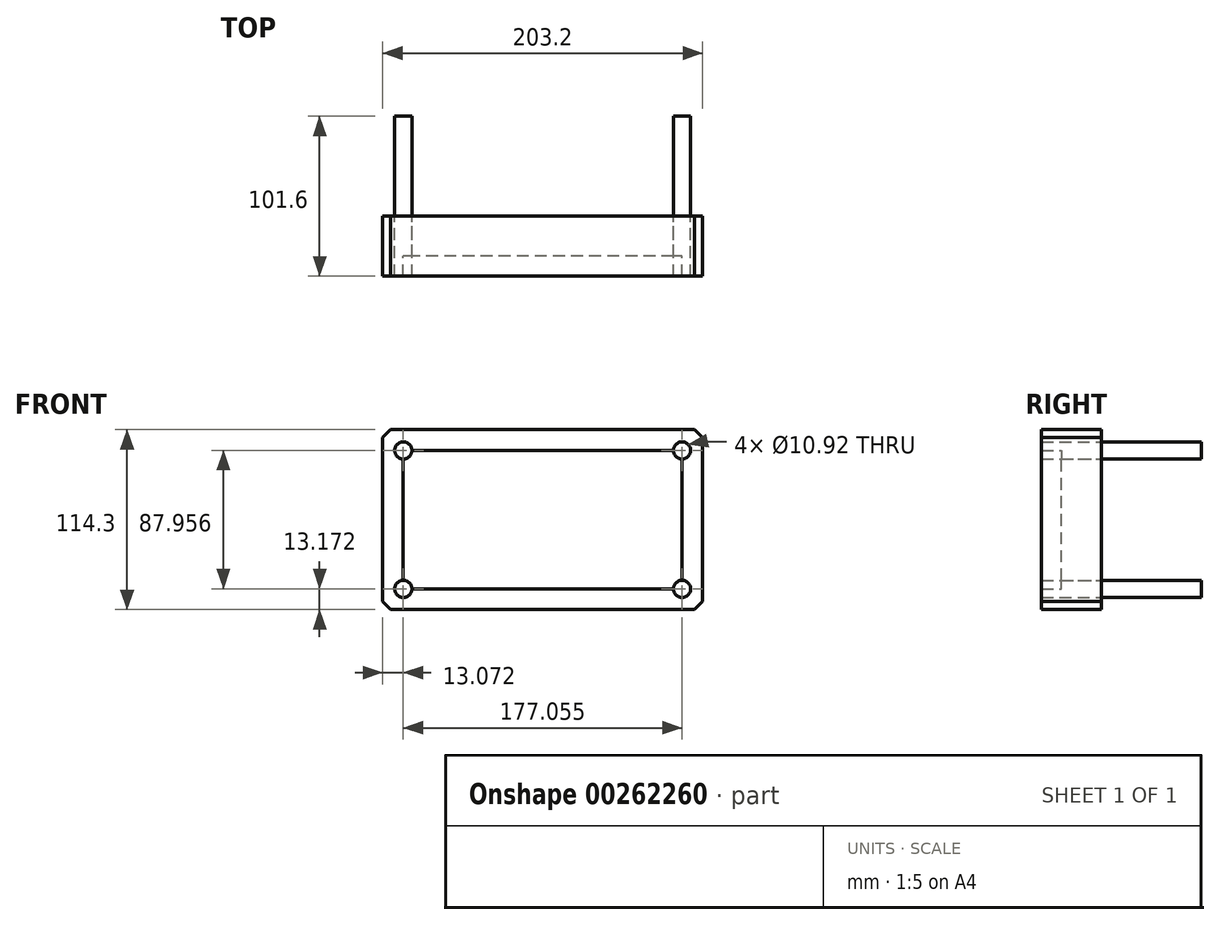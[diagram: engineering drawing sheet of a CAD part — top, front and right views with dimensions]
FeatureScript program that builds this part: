
annotation { "Feature Type Name" : "Feature", "Feature Type Description" : "" }
export const myFeature = defineFeature(function(context is Context, id is Id, definition is map)
    precondition{}
    {
        {
            var Q0;
            Q0=qCreatedBy(makeId("Front.planeOp"),FACE);
            var sketch = newSketch(context, id + "F0", { "sketchPlane" : qUnion([Q0])});
            skLineSegment(sketch, "E0.bottom", {"start": v(101.6, 57.15) * mm, "end": v(-101.6, 57.15) * mm});
            skLineSegment(sketch, "E0.top", {"start": v(101.6, -57.15) * mm, "end": v(-101.6, -57.15) * mm});
            skLineSegment(sketch, "E0.left", {"start": v(101.6, 57.15) * mm, "end": v(101.6, -57.15) * mm});
            skLineSegment(sketch, "E0.right", {"start": v(-101.6, 57.15) * mm, "end": v(-101.6, -57.15) * mm});
            skPoint(sketch, "E0.middle", {"position": v(0, 0) * mm});
            skLineSegment(sketch, "E1.bottom", {"start": v(88.53, -43.98) * mm, "end": v(-88.53, -43.98) * mm});
            skLineSegment(sketch, "E1.top", {"start": v(88.53, 43.98) * mm, "end": v(-88.53, 43.98) * mm});
            skLineSegment(sketch, "E1.left", {"start": v(88.53, -43.98) * mm, "end": v(88.53, 43.98) * mm});
            skLineSegment(sketch, "E1.right", {"start": v(-88.53, -43.98) * mm, "end": v(-88.53, 43.98) * mm});
            skCircle(sketch, "E2", {"center": v(-88.53, -43.98) * mm, "radius": 5.46 * mm});
            skCircle(sketch, "E3", {"center": v(-88.53, 43.98) * mm, "radius": 5.46 * mm});
            skCircle(sketch, "E4", {"center": v(88.53, 43.98) * mm, "radius": 5.46 * mm});
            skCircle(sketch, "E5", {"center": v(88.53, -43.98) * mm, "radius": 5.46 * mm});
            skSolve(sketch);
        }
        {
            var Q0;
            {var subQ5=sQuery(id+"F0.wireOp",EDGE,"E5");var subQ13=sQuery(id+"F0.wireOp",EDGE,"E1.bottom");var subQ14=makeQuery(id+"F0.imprint","INTERSECT",VERTEX,{"derivedFrom":[subQ13,subQ5]});Q0=makeQuery(id+"F0.imprint","IMPRINT",FACE,{"disambiguationData":[TD([[makeQuery(id+"F0.imprint","IMPRINT",EDGE,{"disambiguationData":[TD([[subQ14,-1.0]])],"derivedFrom":subQ13}),-1.0]])]});}
            extrude(context, id + "F1", {"entities" : qUnion([Q0]), "depth" : 25.4 * mm});
        }
        {
            var Q0;
            Q0=makeQuery(id+"F0.imprint","IMPRINT",FACE,{"disambiguationData":[TD([[makeQuery(id+"F0.imprint","IMPRINT",EDGE,{"derivedFrom":sQuery(id+"F0.wireOp",EDGE,"E0.bottom")}),1.0]])]});
            extrude(context, id + "F2", {"entities" : qUnion([Q0]), "operationType" : NewBodyOperationType.ADD, "depth" : 38.1 * mm});
        }
        {
            var Q0;
            {var subQ0=sQuery(id+"F0.wireOp",EDGE,"E1.right");var subQ1=sQuery(id+"F0.wireOp",EDGE,"E1.top");var subQ2=makeQuery(id+"F0.imprint","INTERSECT",VERTEX,{"derivedFrom":[subQ1,subQ0]});Q0=makeQuery(id+"F0.imprint","IMPRINT",FACE,{"disambiguationData":[TD([[makeQuery(id+"F0.imprint","IMPRINT",EDGE,{"disambiguationData":[TD([[subQ2,1.0]])],"derivedFrom":subQ1}),-1.0]])]});}
            var Q1;
            {var subQ0=sQuery(id+"F0.wireOp",EDGE,"E1.right");var subQ1=sQuery(id+"F0.wireOp",EDGE,"E1.bottom");var subQ2=makeQuery(id+"F0.imprint","INTERSECT",VERTEX,{"derivedFrom":[subQ1,subQ0]});Q1=makeQuery(id+"F0.imprint","IMPRINT",FACE,{"disambiguationData":[TD([[makeQuery(id+"F0.imprint","IMPRINT",EDGE,{"disambiguationData":[TD([[subQ2,1.0]])],"derivedFrom":subQ1}),1.0]])]});}
            var Q2;
            {var subQ0=sQuery(id+"F0.wireOp",EDGE,"E1.left");var subQ1=sQuery(id+"F0.wireOp",EDGE,"E1.top");var subQ2=makeQuery(id+"F0.imprint","INTERSECT",VERTEX,{"derivedFrom":[subQ1,subQ0]});Q2=makeQuery(id+"F0.imprint","IMPRINT",FACE,{"disambiguationData":[TD([[makeQuery(id+"F0.imprint","IMPRINT",EDGE,{"disambiguationData":[TD([[subQ2,-1.0]])],"derivedFrom":subQ1}),-1.0]])]});}
            var Q3;
            {var subQ0=sQuery(id+"F0.wireOp",EDGE,"E1.left");var subQ1=sQuery(id+"F0.wireOp",EDGE,"E1.bottom");var subQ2=makeQuery(id+"F0.imprint","INTERSECT",VERTEX,{"derivedFrom":[subQ1,subQ0]});Q3=makeQuery(id+"F0.imprint","IMPRINT",FACE,{"disambiguationData":[TD([[makeQuery(id+"F0.imprint","IMPRINT",EDGE,{"disambiguationData":[TD([[subQ2,-1.0]])],"derivedFrom":subQ1}),1.0]])]});}
            var Q4;
            {var subQ0=sQuery(id+"F0.wireOp",EDGE,"E1.right");var subQ1=sQuery(id+"F0.wireOp",EDGE,"E1.top");var subQ2=makeQuery(id+"F0.imprint","INTERSECT",VERTEX,{"derivedFrom":[subQ1,subQ0]});Q4=makeQuery(id+"F0.imprint","IMPRINT",FACE,{"disambiguationData":[TD([[makeQuery(id+"F0.imprint","IMPRINT",EDGE,{"disambiguationData":[TD([[subQ2,1.0]])],"derivedFrom":subQ1}),1.0]])]});}
            var Q5;
            {var subQ0=sQuery(id+"F0.wireOp",EDGE,"E1.left");var subQ1=sQuery(id+"F0.wireOp",EDGE,"E1.top");var subQ2=makeQuery(id+"F0.imprint","INTERSECT",VERTEX,{"derivedFrom":[subQ1,subQ0]});Q5=makeQuery(id+"F0.imprint","IMPRINT",FACE,{"disambiguationData":[TD([[makeQuery(id+"F0.imprint","IMPRINT",EDGE,{"disambiguationData":[TD([[subQ2,-1.0]])],"derivedFrom":subQ1}),1.0]])]});}
            var Q6;
            {var subQ0=sQuery(id+"F0.wireOp",EDGE,"E1.left");var subQ1=sQuery(id+"F0.wireOp",EDGE,"E1.bottom");var subQ2=makeQuery(id+"F0.imprint","INTERSECT",VERTEX,{"derivedFrom":[subQ1,subQ0]});Q6=makeQuery(id+"F0.imprint","IMPRINT",FACE,{"disambiguationData":[TD([[makeQuery(id+"F0.imprint","IMPRINT",EDGE,{"disambiguationData":[TD([[subQ2,-1.0]])],"derivedFrom":subQ1}),-1.0]])]});}
            var Q7;
            {var subQ0=sQuery(id+"F0.wireOp",EDGE,"E1.right");var subQ1=sQuery(id+"F0.wireOp",EDGE,"E1.bottom");var subQ2=makeQuery(id+"F0.imprint","INTERSECT",VERTEX,{"derivedFrom":[subQ1,subQ0]});Q7=makeQuery(id+"F0.imprint","IMPRINT",FACE,{"disambiguationData":[TD([[makeQuery(id+"F0.imprint","IMPRINT",EDGE,{"disambiguationData":[TD([[subQ2,1.0]])],"derivedFrom":subQ1}),-1.0]])]});}
            extrude(context, id + "F3", {"entities" : qUnion([Q0, Q1, Q2, Q3, Q4, Q5, Q6, Q7]), "depth" : 38.1 * mm});
        }
        {
            var Q0;
            {var subQ0=sQuery(id+"F0.wireOp",EDGE,"E1.right");var subQ1=sQuery(id+"F0.wireOp",EDGE,"E1.bottom");var subQ2=makeQuery(id+"F0.imprint","INTERSECT",VERTEX,{"derivedFrom":[subQ1,subQ0]});Q0=makeQuery(id+"F0.imprint","IMPRINT",FACE,{"disambiguationData":[TD([[makeQuery(id+"F0.imprint","IMPRINT",EDGE,{"disambiguationData":[TD([[subQ2,1.0]])],"derivedFrom":subQ1}),1.0]])]});}
            var Q1;
            {var subQ0=sQuery(id+"F0.wireOp",EDGE,"E1.right");var subQ1=sQuery(id+"F0.wireOp",EDGE,"E1.bottom");var subQ2=makeQuery(id+"F0.imprint","INTERSECT",VERTEX,{"derivedFrom":[subQ1,subQ0]});Q1=makeQuery(id+"F0.imprint","IMPRINT",FACE,{"disambiguationData":[TD([[makeQuery(id+"F0.imprint","IMPRINT",EDGE,{"disambiguationData":[TD([[subQ2,1.0]])],"derivedFrom":subQ1}),-1.0]])]});}
            var Q2;
            {var subQ0=sQuery(id+"F0.wireOp",EDGE,"E1.right");var subQ1=sQuery(id+"F0.wireOp",EDGE,"E1.top");var subQ2=makeQuery(id+"F0.imprint","INTERSECT",VERTEX,{"derivedFrom":[subQ1,subQ0]});Q2=makeQuery(id+"F0.imprint","IMPRINT",FACE,{"disambiguationData":[TD([[makeQuery(id+"F0.imprint","IMPRINT",EDGE,{"disambiguationData":[TD([[subQ2,1.0]])],"derivedFrom":subQ1}),1.0]])]});}
            var Q3;
            {var subQ0=sQuery(id+"F0.wireOp",EDGE,"E1.right");var subQ1=sQuery(id+"F0.wireOp",EDGE,"E1.top");var subQ2=makeQuery(id+"F0.imprint","INTERSECT",VERTEX,{"derivedFrom":[subQ1,subQ0]});Q3=makeQuery(id+"F0.imprint","IMPRINT",FACE,{"disambiguationData":[TD([[makeQuery(id+"F0.imprint","IMPRINT",EDGE,{"disambiguationData":[TD([[subQ2,1.0]])],"derivedFrom":subQ1}),-1.0]])]});}
            var Q4;
            {var subQ0=sQuery(id+"F0.wireOp",EDGE,"E1.left");var subQ1=sQuery(id+"F0.wireOp",EDGE,"E1.bottom");var subQ2=makeQuery(id+"F0.imprint","INTERSECT",VERTEX,{"derivedFrom":[subQ1,subQ0]});Q4=makeQuery(id+"F0.imprint","IMPRINT",FACE,{"disambiguationData":[TD([[makeQuery(id+"F0.imprint","IMPRINT",EDGE,{"disambiguationData":[TD([[subQ2,-1.0]])],"derivedFrom":subQ1}),-1.0]])]});}
            var Q5;
            {var subQ0=sQuery(id+"F0.wireOp",EDGE,"E1.left");var subQ1=sQuery(id+"F0.wireOp",EDGE,"E1.bottom");var subQ2=makeQuery(id+"F0.imprint","INTERSECT",VERTEX,{"derivedFrom":[subQ1,subQ0]});Q5=makeQuery(id+"F0.imprint","IMPRINT",FACE,{"disambiguationData":[TD([[makeQuery(id+"F0.imprint","IMPRINT",EDGE,{"disambiguationData":[TD([[subQ2,-1.0]])],"derivedFrom":subQ1}),1.0]])]});}
            var Q6;
            {var subQ0=sQuery(id+"F0.wireOp",EDGE,"E1.left");var subQ1=sQuery(id+"F0.wireOp",EDGE,"E1.top");var subQ2=makeQuery(id+"F0.imprint","INTERSECT",VERTEX,{"derivedFrom":[subQ1,subQ0]});Q6=makeQuery(id+"F0.imprint","IMPRINT",FACE,{"disambiguationData":[TD([[makeQuery(id+"F0.imprint","IMPRINT",EDGE,{"disambiguationData":[TD([[subQ2,-1.0]])],"derivedFrom":subQ1}),1.0]])]});}
            var Q7;
            {var subQ0=sQuery(id+"F0.wireOp",EDGE,"E1.left");var subQ1=sQuery(id+"F0.wireOp",EDGE,"E1.top");var subQ2=makeQuery(id+"F0.imprint","INTERSECT",VERTEX,{"derivedFrom":[subQ1,subQ0]});Q7=makeQuery(id+"F0.imprint","IMPRINT",FACE,{"disambiguationData":[TD([[makeQuery(id+"F0.imprint","IMPRINT",EDGE,{"disambiguationData":[TD([[subQ2,-1.0]])],"derivedFrom":subQ1}),-1.0]])]});}
            extrude(context, id + "F4", {"entities" : qUnion([Q0, Q1, Q2, Q3, Q4, Q5, Q6, Q7]), "oppositeDirection" : true, "depth" : 63.5 * mm});
        }
        {
            var Q0;
            Q0=makeQuery(id+"F2.opExtrude","SWEPT_EDGE",EDGE,{"disambiguationData":[OSD([sQuery(id+"F0.wireOp",EDGE,"E0.top"),sQuery(id+"F0.wireOp",EDGE,"E0.right")])]});
            var Q1;
            Q1=makeQuery(id+"F2.opExtrude","SWEPT_EDGE",EDGE,{"disambiguationData":[OSD([sQuery(id+"F0.wireOp",EDGE,"E0.top"),sQuery(id+"F0.wireOp",EDGE,"E0.left")])]});
            var Q2;
            Q2=makeQuery(id+"F2.opExtrude","SWEPT_EDGE",EDGE,{"disambiguationData":[OSD([sQuery(id+"F0.wireOp",EDGE,"E0.bottom"),sQuery(id+"F0.wireOp",EDGE,"E0.left")])]});
            var Q3;
            Q3=makeQuery(id+"F2.opExtrude","SWEPT_EDGE",EDGE,{"disambiguationData":[OSD([sQuery(id+"F0.wireOp",EDGE,"E0.bottom"),sQuery(id+"F0.wireOp",EDGE,"E0.right")])]});
            chamfer(context, id + "F5", {"entities" : qUnion([Q0, Q1, Q2, Q3]), "width" : 5.08 * mm, "tangentPropagation" : true});
        }
    });
